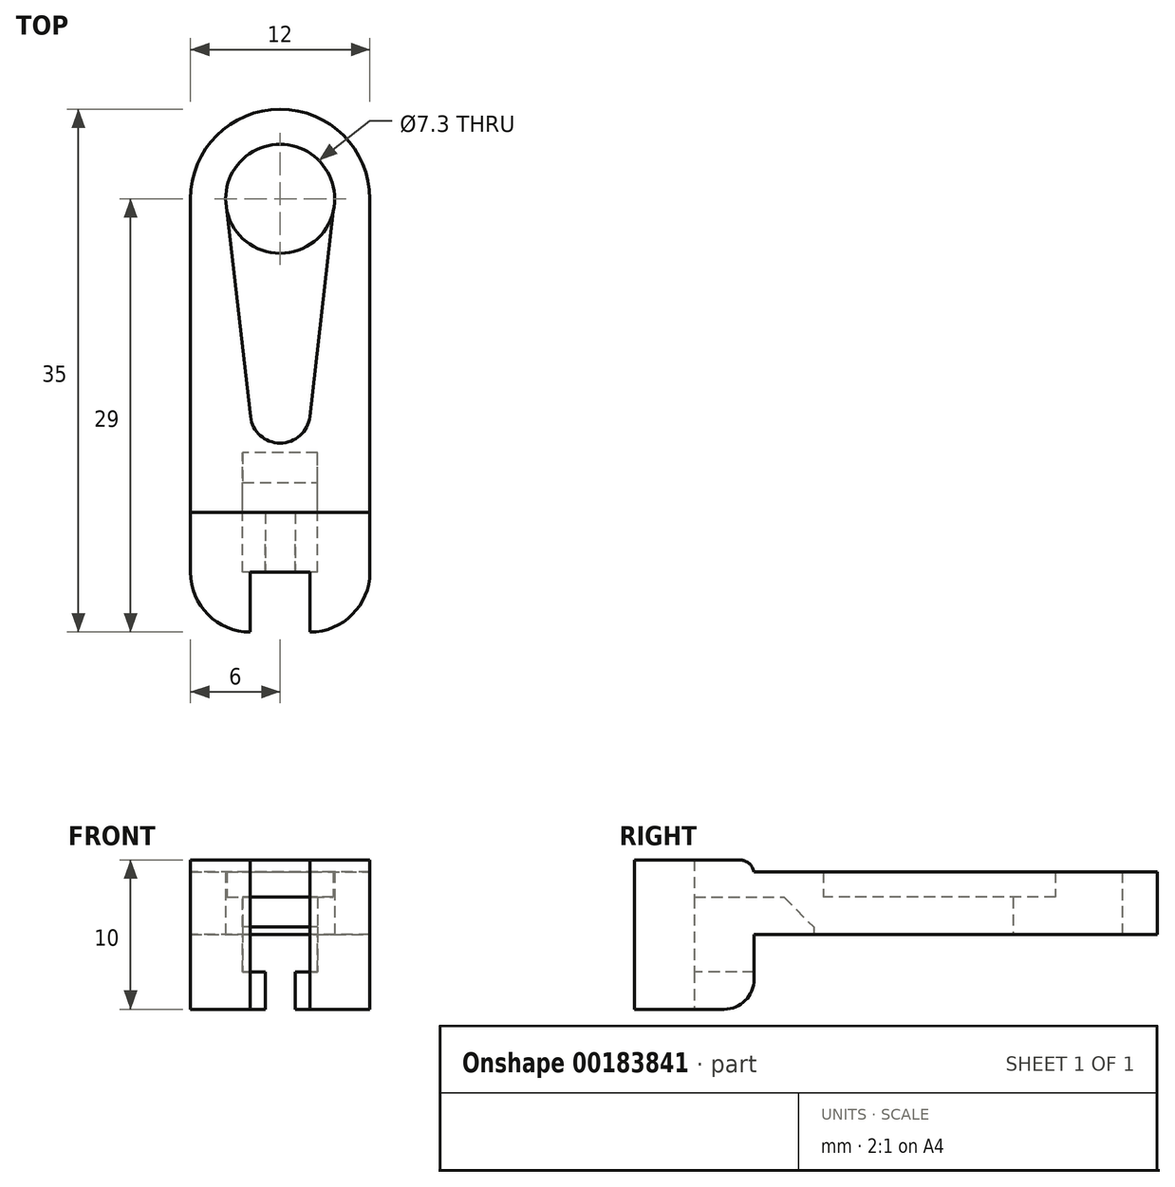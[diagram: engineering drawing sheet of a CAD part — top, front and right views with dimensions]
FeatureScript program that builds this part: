
annotation { "Feature Type Name" : "Feature", "Feature Type Description" : "" }
export const myFeature = defineFeature(function(context is Context, id is Id, definition is map)
    precondition{}
    {
        {
            var Q0;
            Q0=qCreatedBy(makeId("Top.planeOp"),FACE);
            var sketch = newSketch(context, id + "F0", { "sketchPlane" : qUnion([Q0])});
            skLineSegment(sketch, "E0.bottom", {"start": v(-6, 14.5) * mm, "end": v(6, 14.5) * mm});
            skLineSegment(sketch, "E0.top", {"start": v(-6, -14.5) * mm, "end": v(6, -14.5) * mm});
            skLineSegment(sketch, "E0.left", {"start": v(-6, 14.5) * mm, "end": v(-6, -14.5) * mm});
            skLineSegment(sketch, "E0.right", {"start": v(6, 14.5) * mm, "end": v(6, -14.5) * mm});
            skPoint(sketch, "E0.middle", {"position": v(0, 0) * mm});
            skCircle(sketch, "E1", {"center": v(0, 0.15) * mm, "radius": 2 * mm});
            skCircle(sketch, "E2", {"center": v(0, 14.5) * mm, "radius": 3.65 * mm});
            skLineSegment(sketch, "E3", {"start": v(0, 18.15) * mm, "end": v(0, -1.85) * mm});
            skArc(sketch, "E4", {"start": v(6, 14.5) * mm, "mid": v(0, 20.5) * mm, "end": v(-6, 14.5) * mm});
            skLineSegment(sketch, "E5", {"start": v(-3.65, 14.5) * mm, "end": v(-1.83, -1.42) * mm});
            skLineSegment(sketch, "E6", {"start": v(3.65, 14.5) * mm, "end": v(1.73, -2.29) * mm});
            skLineSegment(sketch, "E7.bottom", {"start": v(0, -14.5) * mm, "end": v(2, -14.5) * mm});
            skLineSegment(sketch, "E7.top", {"start": v(0, -10.5) * mm, "end": v(2, -10.5) * mm});
            skLineSegment(sketch, "E7.right", {"start": v(2, -14.5) * mm, "end": v(2, -10.5) * mm});
            skLineSegment(sketch, "E8.bottom", {"start": v(0, -14.5) * mm, "end": v(-2, -14.5) * mm});
            skLineSegment(sketch, "E8.top", {"start": v(0, -10.5) * mm, "end": v(-2, -10.5) * mm});
            skLineSegment(sketch, "E8.right", {"start": v(-2, -14.5) * mm, "end": v(-2, -10.5) * mm});
            skArc(sketch, "E9", {"start": v(-6, -10.5) * mm, "mid": v(-4.83, -13.33) * mm, "end": v(-2, -14.5) * mm});
            skArc(sketch, "E10.MirrorCS", {"start": v(6, -10.5) * mm, "mid": v(4.83, -13.33) * mm, "end": v(2, -14.5) * mm});
            skLineSegment(sketch, "E11", {"start": v(6, -6.5) * mm, "end": v(-6, -6.5) * mm});
            skSolve(sketch);
        }
        {
            var Q0;
            {var subQ5=sQuery(id+"F0.wireOp",EDGE,"E4");Q0=makeQuery(id+"F0.imprint","IMPRINT",FACE,{"disambiguationData":[TD([[makeQuery(id+"F0.imprint","IMPRINT",EDGE,{"derivedFrom":subQ5}),1.0]])]});}
            var Q1;
            Q1=makeQuery(id+"F0.imprint","IMPRINT",FACE,{"disambiguationData":[TD([[makeQuery(id+"F0.imprint","IMPRINT",EDGE,{"derivedFrom":sQuery(id+"F0.wireOp",EDGE,"E7.top")}),1.0]])]});
            var Q2;
            {var subQ17=sQuery(id+"F0.wireOp",EDGE,"E11");Q2=makeQuery(id+"F0.imprint","IMPRINT",FACE,{"disambiguationData":[TD([[makeQuery(id+"F0.imprint","IMPRINT",EDGE,{"derivedFrom":subQ17}),-1.0]])]});}
            extrude(context, id + "F1", {"entities" : qUnion([Q0, Q1, Q2]), "depth" : 4.2 * mm});
        }
        {
            var Q0;
            {var subQ0=sQuery(id+"F0.wireOp",EDGE,"E5");var subQ1=sQuery(id+"F0.wireOp",EDGE,"E1");var subQ2=makeQuery(id+"F0.imprint","INTERSECT",VERTEX,{"derivedFrom":[subQ1,subQ0]});Q0=makeQuery(id+"F0.imprint","IMPRINT",FACE,{"disambiguationData":[TD([[makeQuery(id+"F0.imprint","IMPRINT",EDGE,{"disambiguationData":[TD([[subQ2,1.0]])],"derivedFrom":subQ1}),-1.0]])]});}
            var Q1;
            {var subQ0=sQuery(id+"F0.wireOp",EDGE,"E6");var subQ1=sQuery(id+"F0.wireOp",EDGE,"E1");var subQ2=makeQuery(id+"F0.imprint","INTERSECT",VERTEX,{"derivedFrom":[subQ1,subQ0]});Q1=makeQuery(id+"F0.imprint","IMPRINT",FACE,{"disambiguationData":[TD([[makeQuery(id+"F0.imprint","IMPRINT",EDGE,{"disambiguationData":[TD([[subQ2,-1.0]])],"derivedFrom":subQ1}),-1.0]])]});}
            var Q2;
            {var subQ0=sQuery(id+"F0.wireOp",EDGE,"E1");var subQ1=makeQuery(id+"F0.imprint","INTERSECT",VERTEX,{"derivedFrom":[subQ0,sQuery(id+"F0.wireOp",EDGE,"E5")]});Q2=makeQuery(id+"F0.imprint","IMPRINT",FACE,{"disambiguationData":[TD([[makeQuery(id+"F0.imprint","IMPRINT",EDGE,{"disambiguationData":[TD([[subQ1,1.0]])],"derivedFrom":subQ0}),1.0]])]});}
            var Q3;
            {var subQ0=sQuery(id+"F0.wireOp",EDGE,"E3");var subQ1=sQuery(id+"F0.wireOp",EDGE,"E1");var subQ2=makeQuery(id+"F0.imprint","INTERSECT",VERTEX,{"disambiguationData":[OD(0.0)],"derivedFrom":[subQ1,subQ0]});Q3=makeQuery(id+"F0.imprint","IMPRINT",FACE,{"disambiguationData":[TD([[makeQuery(id+"F0.imprint","IMPRINT",EDGE,{"disambiguationData":[TD([[subQ2,-1.0]])],"derivedFrom":subQ1}),1.0]])]});}
            extrude(context, id + "F2", {"entities" : qUnion([Q0, Q1, Q2, Q3]), "operationType" : NewBodyOperationType.ADD, "depth" : 2.5 * mm});
        }
        {
            var Q0;
            Q0=makeQuery(id+"F0.imprint","IMPRINT",FACE,{"disambiguationData":[TD([[makeQuery(id+"F0.imprint","IMPRINT",EDGE,{"derivedFrom":sQuery(id+"F0.wireOp",EDGE,"E7.top")}),1.0]])]});
            extrude(context, id + "F3", {"entities" : qUnion([Q0]), "operationType" : NewBodyOperationType.ADD, "depth" : 5 * mm, "hasSecondDirection" : true, "secondDirectionOppositeDirection" : true, "secondDirectionDepth" : 5 * mm});
        }
        {
            var Q0;
            {var subQ0=sQuery(id+"F0.wireOp",EDGE,"E6");var subQ1=sQuery(id+"F0.wireOp",EDGE,"E5");var subQ2=sQuery(id+"F0.wireOp",EDGE,"E2");var subQ3=sQuery(id+"F0.wireOp",EDGE,"E1");var subQ12=sQuery(id+"F0.wireOp",EDGE,"E11");Q0=makeQuery(id+"F3.boolean.opBoolean","SPLIT",FACE,{"disambiguationData":[TD([makeQuery(id+"F2.opExtrude","CAP_FACE",FACE,{"disambiguationData":[OSD([subQ3,subQ2,subQ1,subQ0])],"isStart":true})])],"derivedFrom":makeQuery(id+"F3.opExtrude","SWEPT_FACE",FACE,{"disambiguationData":[OSD([subQ12])]})});}
            var sketch = newSketch(context, id + "F4", { "sketchPlane" : qUnion([Q0])});
            skLineSegment(sketch, "E12.bottom", {"start": v(-2.5, 2.5) * mm, "end": v(2.5, 2.5) * mm});
            skLineSegment(sketch, "E12.top", {"start": v(-2.5, -2.5) * mm, "end": v(2.5, -2.5) * mm});
            skLineSegment(sketch, "E12.left", {"start": v(-2.5, 2.5) * mm, "end": v(-2.5, -2.5) * mm});
            skLineSegment(sketch, "E12.right", {"start": v(2.5, 2.5) * mm, "end": v(2.5, -2.5) * mm});
            skPoint(sketch, "E12.middle", {"position": v(0, 0) * mm});
            skSolve(sketch);
        }
        {
            var Q0;
            Q0 = qSketchRegion(id + "F4", true);
            extrude(context, id + "F5", {"entities" : qUnion([Q0]), "operationType" : NewBodyOperationType.REMOVE, "oppositeDirection" : true, "depth" : 4 * mm, "hasSecondDirection" : true, "secondDirectionOppositeDirection" : false, "secondDirectionDepth" : 4 * mm});
        }
        {
            var Q0;
            Q0=makeQuery(id+"F5.boolean.opBoolean","COPY",EDGE,{"derivedFrom":makeQuery(id+"F5.opExtrude","CAP_EDGE",EDGE,{"disambiguationData":[OSD([sQuery(id+"F4.wireOp",EDGE,"E12.bottom")])],"isStart":true})});
            chamfer(context, id + "F6", {"entities" : qUnion([Q0]), "width" : 2 * mm, "tangentPropagation" : true});
        }
        {
            var Q0;
            {var subQ2=sQuery(id+"F0.wireOp",EDGE,"E8.top");var subQ3=sQuery(id+"F0.wireOp",EDGE,"E7.top");var subQ4=sQuery(id+"F4.wireOp",EDGE,"E12.top");Q0=makeQuery(id+"F5.boolean.opBoolean","SPLIT",FACE,{"disambiguationData":[TD([makeQuery(id+"F5.opExtrude","SWEPT_FACE",FACE,{"disambiguationData":[OSD([subQ4])]})])],"derivedFrom":makeQuery(id+"F3.boolean.opBoolean","MERGE",FACE,{"derivedFrom":[makeQuery(id+"F1.opExtrude","SWEPT_FACE",FACE,{"disambiguationData":[OSD([subQ3,subQ2])]}),makeQuery(id+"F3.opExtrude","SWEPT_FACE",FACE,{"disambiguationData":[OSD([subQ3,subQ2])]})]})});}
            var sketch = newSketch(context, id + "F7", { "sketchPlane" : qUnion([Q0])});
            skSolve(sketch);
        }
        {
            var Q0;
            {var subQ0=sQuery(id+"F0.wireOp",EDGE,"E8.top");var subQ1=sQuery(id+"F0.wireOp",EDGE,"E7.top");Q0=makeQuery(id+"F7.imprint","IMPRINT",FACE,{"disambiguationData":[TD([[makeQuery(id+"F7.imprint","IMPRINT",EDGE,{"derivedFrom":makeQuery(id+"F3.opExtrude","CAP_EDGE",EDGE,{"disambiguationData":[OSD([subQ1,subQ0])],"isStart":true})}),-1.0]])]});}
            extrude(context, id + "F8", {"entities" : qUnion([Q0]), "operationType" : NewBodyOperationType.REMOVE, "oppositeDirection" : true, "depth" : 25 * mm});
        }
        {
            var Q0;
            {var subQ0=sQuery(id+"F0.wireOp",EDGE,"E0.right");var subQ1=sQuery(id+"F0.wireOp",EDGE,"E11");Q0=makeQuery(id+"F8.boolean.opBoolean","SPLIT",EDGE,{"disambiguationData":[TD([makeQuery(id+"F1.opExtrude","SWEPT_FACE",FACE,{"disambiguationData":[OSD([subQ0])]})])],"derivedFrom":makeQuery(id+"F3.opExtrude","CAP_EDGE",EDGE,{"disambiguationData":[OSD([subQ1])],"isStart":true})});}
            var Q1;
            {var subQ1=sQuery(id+"F0.wireOp",EDGE,"E11");var subQ3=sQuery(id+"F0.wireOp",EDGE,"E0.left");Q1=makeQuery(id+"F8.boolean.opBoolean","SPLIT",EDGE,{"disambiguationData":[TD([makeQuery(id+"F1.opExtrude","SWEPT_FACE",FACE,{"disambiguationData":[OSD([subQ3])]})])],"derivedFrom":makeQuery(id+"F3.opExtrude","CAP_EDGE",EDGE,{"disambiguationData":[OSD([subQ1])],"isStart":true})});}
            fillet(context, id + "F9", {"entities" : qUnion([Q0, Q1]), "radius" : 2 * mm, "tangentPropagation" : true, "allowEdgeOverflow" : false});
        }
        {
            var Q0;
            {var subQ0=sQuery(id+"F0.wireOp",EDGE,"E8.right");Q0=makeQuery(id+"F8.boolean.opBoolean","MERGE",FACE,{"derivedFrom":[makeQuery(id+"F3.boolean.opBoolean","MERGE",FACE,{"derivedFrom":[makeQuery(id+"F1.opExtrude","SWEPT_FACE",FACE,{"disambiguationData":[OSD([subQ0])]}),makeQuery(id+"F3.opExtrude","SWEPT_FACE",FACE,{"disambiguationData":[OSD([subQ0])]})]}),makeQuery(id+"F8.opExtrude","SWEPT_FACE",FACE,{"disambiguationData":[OSD([sQuery(id+"F0.wireOp",EDGE,"E8.top"),subQ0])]})]});}
            var sketch = newSketch(context, id + "F10", { "sketchPlane" : qUnion([Q0])});
            skLineSegment(sketch, "E13", {"start": v(-10.5, -2.5) * mm, "end": v(-10.5, -5) * mm});
            skSolve(sketch);
        }
        {
            var Q0;
            Q0 = qSketchRegion(id + "F10", true);
            var Q1;
            {var subQ21=sQuery(id+"F10.wireOp",EDGE,"E13");Q1=makeQuery(id+"F10.imprint","IMPRINT",FACE,{"disambiguationData":[TD([[makeQuery(id+"F10.imprint","IMPRINT",EDGE,{"derivedFrom":subQ21}),1.0]])]});}
            extrude(context, id + "F11", {"entities" : qUnion([Q0, Q1]), "operationType" : NewBodyOperationType.ADD, "depth" : 1 * mm});
        }
        {
            var Q0;
            {var subQ0=sQuery(id+"F0.wireOp",EDGE,"E7.right");Q0=makeQuery(id+"F8.boolean.opBoolean","MERGE",FACE,{"derivedFrom":[makeQuery(id+"F3.boolean.opBoolean","MERGE",FACE,{"derivedFrom":[makeQuery(id+"F1.opExtrude","SWEPT_FACE",FACE,{"disambiguationData":[OSD([subQ0])]}),makeQuery(id+"F3.opExtrude","SWEPT_FACE",FACE,{"disambiguationData":[OSD([subQ0])]})]}),makeQuery(id+"F8.opExtrude","SWEPT_FACE",FACE,{"disambiguationData":[OSD([sQuery(id+"F0.wireOp",EDGE,"E7.top"),subQ0])]})]});}
            var sketch = newSketch(context, id + "F12", { "sketchPlane" : qUnion([Q0])});
            skLineSegment(sketch, "E14", {"start": v(10.5, -2.5) * mm, "end": v(10.5, -5) * mm});
            skSolve(sketch);
        }
        {
            var Q0;
            {var subQ21=sQuery(id+"F12.wireOp",EDGE,"E14");Q0=makeQuery(id+"F12.imprint","IMPRINT",FACE,{"disambiguationData":[TD([[makeQuery(id+"F12.imprint","IMPRINT",EDGE,{"derivedFrom":subQ21}),-1.0]])]});}
            extrude(context, id + "F13", {"entities" : qUnion([Q0]), "operationType" : NewBodyOperationType.ADD, "depth" : 1 * mm});
        }
        {
            var Q0;
            Q0=makeQuery(id+"F3.opExtrude","CAP_EDGE",EDGE,{"disambiguationData":[OSD([sQuery(id+"F0.wireOp",EDGE,"E11")])],"isStart":false});
            fillet(context, id + "F14", {"entities" : qUnion([Q0]), "radius" : 1 * mm, "tangentPropagation" : true, "allowEdgeOverflow" : false});
        }
    });
